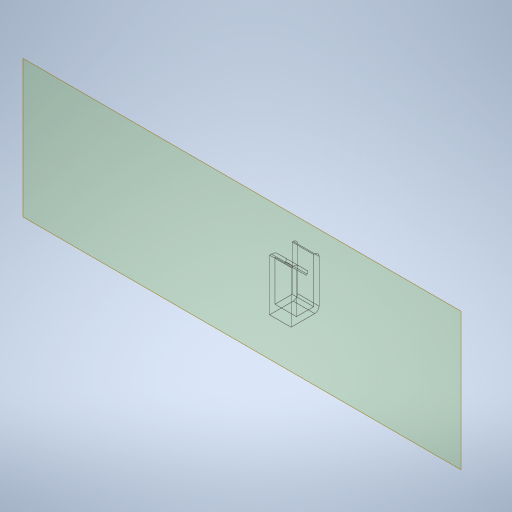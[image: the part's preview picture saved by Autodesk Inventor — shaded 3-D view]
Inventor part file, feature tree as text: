
AUTODESK INVENTOR PART (.ipt)
format: ipt  version: 2024 (Build 280153000, 153)  size: 648,192 bytes
history: native  units: mm
features: extrude x4, sketch x4, fillet x3, projected_geometry x3, other x3, plane x1
ambient origin geometry x8: Origin, YZ Plane, XZ Plane, XY Plane, X Axis, Y Axis, Z Axis, Center Point
bodies: Solid1 (feature_tree)
feature tree (18):
  plane  "Work Plane1"
  extrude  "Extrusion1"  Depth=10.0mm
  extrude  "Extrusion2"  Depth=4.0mm
  extrude  "Extrusion3"  Depth=3.0mm
  extrude  "Extrusion4"  Depth=2.5mm TaperAngle=0.0deg
  fillet  "Fillet1"  Radius=8.0mm
  fillet  "Fillet2"  [1 undecoded]
  fillet  "Fillet3"  Radius=1.5mm
  sketch  "Sketch1"  dims[d0=20.0mm d1=10.0mm]
  sketch  "Sketch2"  dims[d2=177.305983mm d3=4.0mm]
  projected_geometry  "Projected Loop1"
  sketch  "Sketch3"  dims[d4=2.5mm d5=0.0mm d6=3.0mm]
  projected_geometry  "Projected Loop2"
  projected_geometry  "Projected Loop3"
  sketch  "Sketch4"  dims[d7=8.0mm d8=0.0mm d9=2.5mm d10=0.0mm d11=8.0mm d12=45.0deg d13=1.5mm d14=3.0mm d15=0.0mm d16=2.0mm d17=4.0mm d18=1.0mm]
  other  "<userpath>\Documents\Inventor\robot arm\arms\arms.iam"
  other  "arms.iam"
  other  "arm middle:1"
note: 1 required parameter value undecoded (feature->parameter linkage not recoverable at this tier; creation-order binding heuristic only, values carry confidence <= 0.55)
